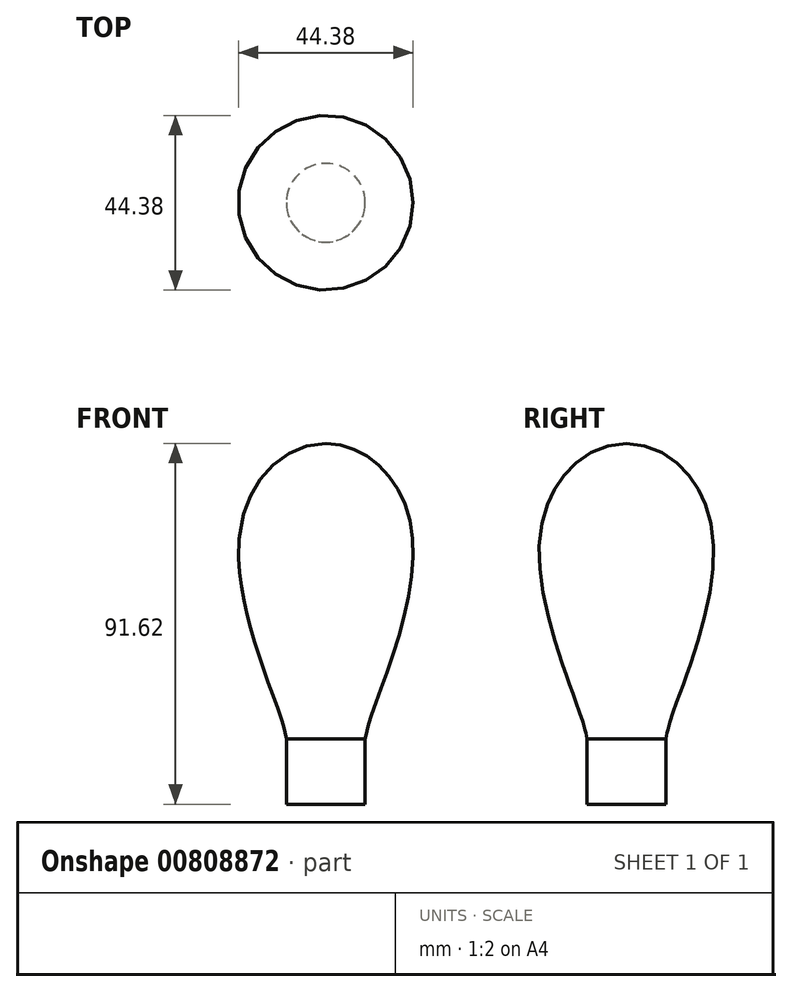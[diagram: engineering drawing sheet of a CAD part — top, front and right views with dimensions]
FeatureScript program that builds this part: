
annotation { "Feature Type Name" : "Feature", "Feature Type Description" : "" }
export const myFeature = defineFeature(function(context is Context, id is Id, definition is map)
    precondition{}
    {
        {
            var Q0;
            Q0=qCreatedBy(makeId("Front.planeOp"),FACE);
            var sketch = newSketch(context, id + "F0", { "sketchPlane" : qUnion([Q0])});
            skLineSegment(sketch, "E0.bottom", {"start": v(-5, 8.31) * mm, "end": v(5, 8.31) * mm});
            skLineSegment(sketch, "E0.top", {"start": v(-5, -8.31) * mm, "end": v(5, -8.31) * mm});
            skLineSegment(sketch, "E0.left", {"start": v(-5, 8.31) * mm, "end": v(-5, -8.31) * mm});
            skLineSegment(sketch, "E0.right", {"start": v(5, 8.31) * mm, "end": v(5, -8.31) * mm});
            skPoint(sketch, "E0.middle", {"position": v(0, 0) * mm});
            skLineSegment(sketch, "E1", {"start": v(-5, 8.31) * mm, "end": v(-5, 83.31) * mm});
            skFitSpline(sketch, "E2", {"points": [v(-5, 83.31) * mm, v(16.96, 60.08) * mm, v(6.08, 12.65) * mm, v(5, 8.31) * mm], "startDerivative": vector(86.5, -0.7) * mm, "endDerivative": vector(-5.34, -14.42) * mm});
            skSolve(sketch);
        }
        {
            var Q0;
            Q0=makeQuery(id+"F0.imprint","IMPRINT",FACE,{"disambiguationData":[TD([[makeQuery(id+"F0.imprint","IMPRINT",EDGE,{"derivedFrom":sQuery(id+"F0.wireOp",EDGE,"E0.bottom")}),1.0]])]});
            var Q1;
            Q1=makeQuery(id+"F0.imprint","IMPRINT",FACE,{"disambiguationData":[TD([[makeQuery(id+"F0.imprint","IMPRINT",EDGE,{"derivedFrom":sQuery(id+"F0.wireOp",EDGE,"E0.bottom")}),-1.0]])]});
            var Q2;
            Q2=sQuery(id+"F0.wireOp",EDGE,"E1");
            revolve(context, id + "F1", {"surfaceOperationType" : NewSurfaceOperationType.NEW, "entities" : qUnion([Q0, Q1]), "axis" : qUnion([Q2]), "revolveType" : RevolveType.FULL});
        }
    });
